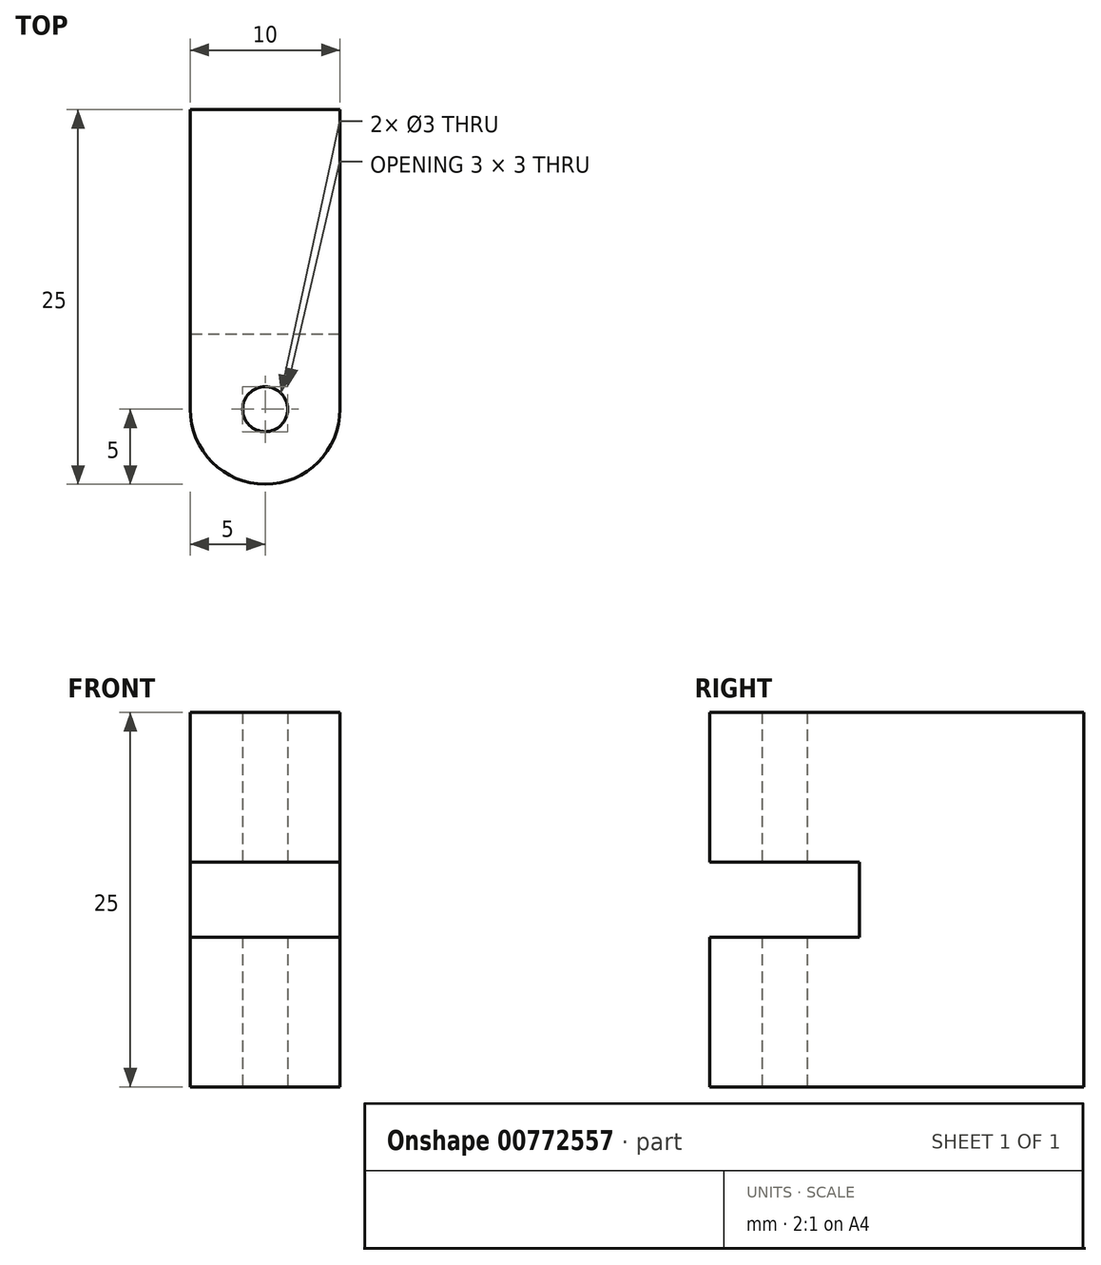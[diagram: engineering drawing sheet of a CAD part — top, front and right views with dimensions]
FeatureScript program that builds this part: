
annotation { "Feature Type Name" : "Feature", "Feature Type Description" : "" }
export const myFeature = defineFeature(function(context is Context, id is Id, definition is map)
    precondition{}
    {
        {
            var Q0;
            Q0=qCreatedBy(makeId("Top.planeOp"),FACE);
            var sketch = newSketch(context, id + "F0", { "sketchPlane" : qUnion([Q0])});
            skCircle(sketch, "E0", {"center": v(0, 0) * mm, "radius": 5 * mm});
            skLineSegment(sketch, "E1.bottom", {"start": v(-5, 0) * mm, "end": v(5, 0) * mm});
            skLineSegment(sketch, "E1.top", {"start": v(-5, 20) * mm, "end": v(5, 20) * mm});
            skLineSegment(sketch, "E1.left", {"start": v(-5, 0) * mm, "end": v(-5, 20) * mm});
            skLineSegment(sketch, "E1.right", {"start": v(5, 0) * mm, "end": v(5, 20) * mm});
            skCircle(sketch, "E2", {"center": v(0, 0) * mm, "radius": 1.5 * mm});
            skSolve(sketch);
        }
        {
            var Q0;
            Q0 = qSketchRegion(id + "F0", true);
            extrude(context, id + "F1", {"entities" : qUnion([Q0]), "depth" : 25 * mm, "offsetDistance" : 25 * mm});
        }
        {
            var Q0;
            Q0=makeQuery(id+"F1.opExtrude","SWEPT_FACE",FACE,{"disambiguationData":[OSD([sQuery(id+"F0.wireOp",EDGE,"E1.right")])]});
            var sketch = newSketch(context, id + "F2", { "sketchPlane" : qUnion([Q0])});
            skLineSegment(sketch, "E3", {"start": v(0, 0) * mm, "end": v(0, 10) * mm, "construction": true});
            skLineSegment(sketch, "E4", {"start": v(0, 10) * mm, "end": v(5, 10) * mm, "construction": true});
            skLineSegment(sketch, "E5.bottom", {"start": v(5, 10) * mm, "end": v(-10, 10) * mm});
            skLineSegment(sketch, "E5.top", {"start": v(5, 15) * mm, "end": v(-10, 15) * mm});
            skLineSegment(sketch, "E5.left", {"start": v(5, 10) * mm, "end": v(5, 15) * mm});
            skLineSegment(sketch, "E5.right", {"start": v(-10, 10) * mm, "end": v(-10, 15) * mm});
            skSolve(sketch);
        }
        {
            var Q0;
            Q0 = qSketchRegion(id + "F2", true);
            extrude(context, id + "F3", {"entities" : qUnion([Q0]), "operationType" : NewBodyOperationType.REMOVE, "endBound" : BoundingType.SYMMETRIC, "depth" : 25 * mm, "offsetDistance" : 25 * mm});
        }
    });
